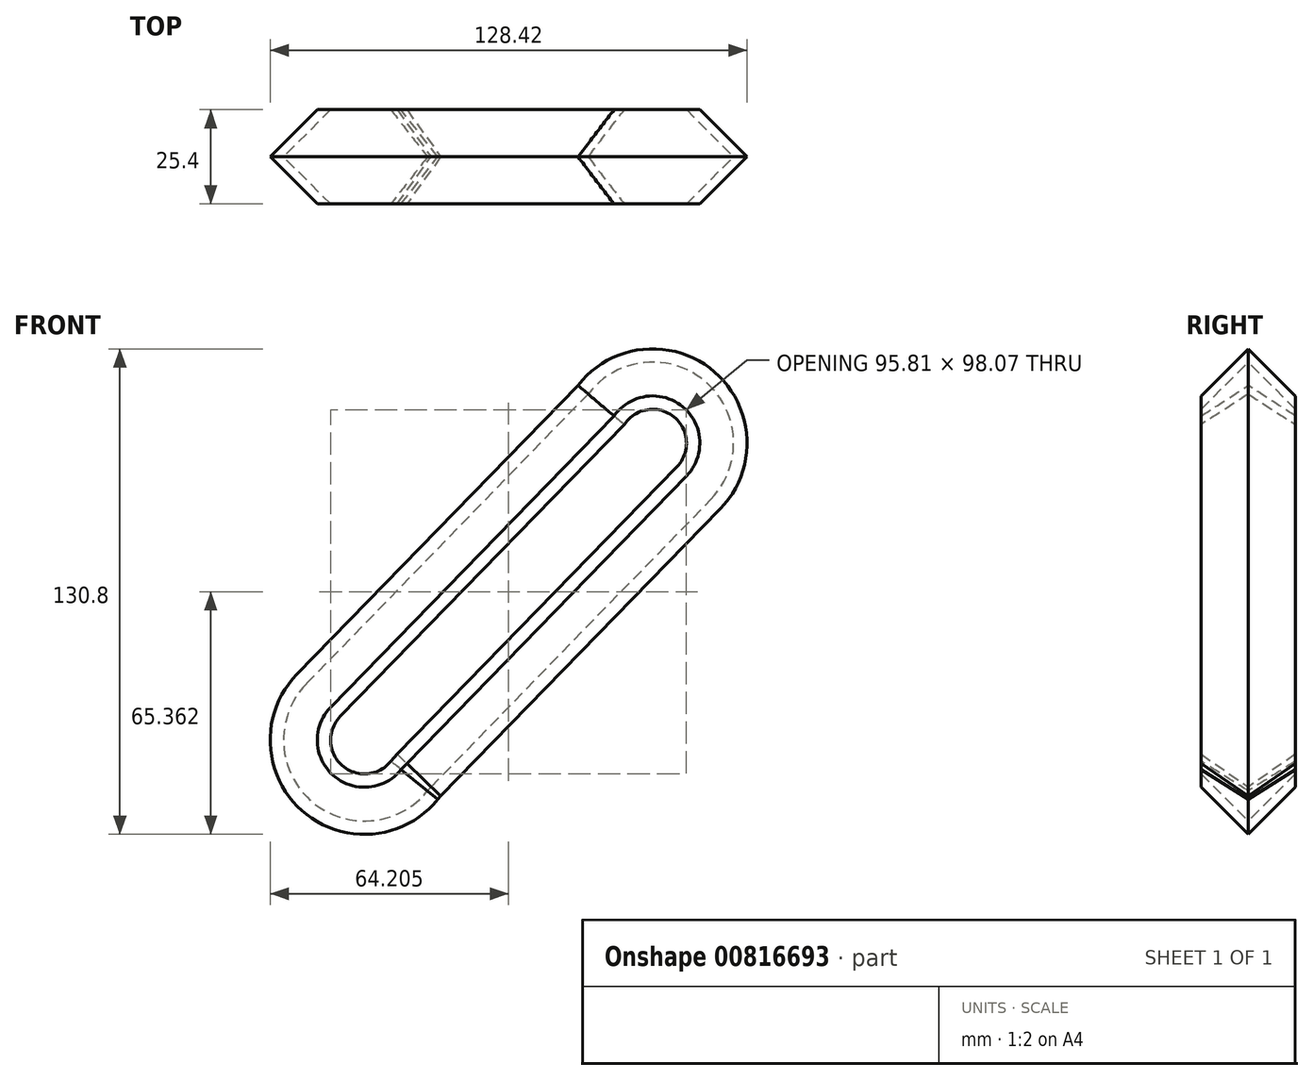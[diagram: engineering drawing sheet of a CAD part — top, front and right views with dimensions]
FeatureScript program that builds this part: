
annotation { "Feature Type Name" : "Feature", "Feature Type Description" : "" }
export const myFeature = defineFeature(function(context is Context, id is Id, definition is map)
    precondition{}
    {
        {
            var Q0;
            Q0=qCreatedBy(makeId("Front.planeOp"),FACE);
            var sketch = newSketch(context, id + "F0", { "sketchPlane" : qUnion([Q0])});
            skCircle(sketch, "E0", {"center": v(-40.16, -39.3) * mm, "radius": 25.4 * mm});
            skCircle(sketch, "E1", {"center": v(37.46, 40.69) * mm, "radius": 25.4 * mm});
            skLineSegment(sketch, "E2", {"start": v(-24.05, -58.95) * mm, "end": v(55.66, 22.97) * mm});
            skLineSegment(sketch, "E3", {"start": v(-58.36, -21.6) * mm, "end": v(21.35, 60.32) * mm});
            skSolve(sketch);
        }
        {
            var Q0;
            Q0 = qSketchRegion(id + "F0", true);
            extrude(context, id + "F1", {"entities" : qUnion([Q0]), "depth" : 25.4 * mm, "offsetDistance" : 25.4 * mm});
        }
        {
            var Q0;
            Q0=makeQuery(id+"F1.opExtrude","SWEPT_FACE",FACE,{"disambiguationData":[OSD([sQuery(id+"F0.wireOp",EDGE,"E2")])]});
            var Q1;
            Q1=makeQuery(id+"F1.opExtrude","CAP_FACE",FACE,{"disambiguationData":[OSD([sQuery(id+"F0.wireOp",EDGE,"E0"),sQuery(id+"F0.wireOp",EDGE,"E1"),sQuery(id+"F0.wireOp",EDGE,"E2"),sQuery(id+"F0.wireOp",EDGE,"E3")])],"isStart":false});
            chamfer(context, id + "F2", {"entities" : qUnion([Q0, Q1]), "width" : 12.7 * mm, "tangentPropagation" : true});
        }
        {
            var Q0;
            Q0=makeQuery(id+"F1.opExtrude","CAP_FACE",FACE,{"disambiguationData":[OSD([sQuery(id+"F0.wireOp",EDGE,"E0"),sQuery(id+"F0.wireOp",EDGE,"E1"),sQuery(id+"F0.wireOp",EDGE,"E2"),sQuery(id+"F0.wireOp",EDGE,"E3")])],"isStart":true});
            var Q1;
            Q1=makeQuery(id+"F1.opExtrude","CAP_FACE",FACE,{"disambiguationData":[OSD([sQuery(id+"F0.wireOp",EDGE,"E0"),sQuery(id+"F0.wireOp",EDGE,"E1"),sQuery(id+"F0.wireOp",EDGE,"E2"),sQuery(id+"F0.wireOp",EDGE,"E3")])],"isStart":false});
            shell(context, id + "F3", {"entities" : qUnion([Q0, Q1]), "thickness" : 2.54 * mm});
        }
    });
